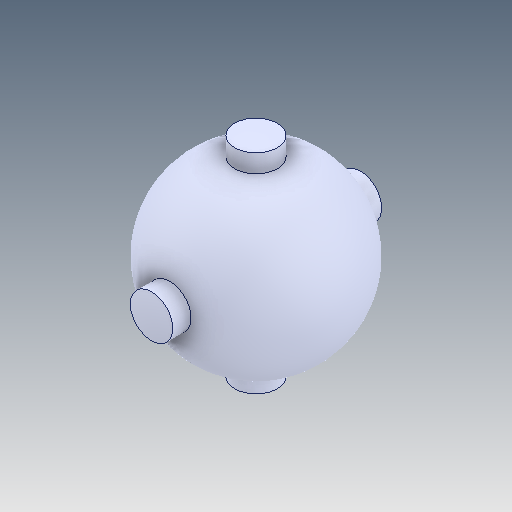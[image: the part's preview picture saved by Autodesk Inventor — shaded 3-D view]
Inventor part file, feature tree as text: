
AUTODESK INVENTOR PART (.ipt)
format: ipt  version: 2020 (Build 240168000, 168)  size: 141,312 bytes
history: mixed  units: in
note: dims shown in document units (in); Inventor stores cm internally (conversion verified against a paired STEP export)
features: revolve x1, imported_body x1
ambient origin geometry x8: Origin, YZ Plane, XZ Plane, XY Plane, X Axis, Y Axis, Z Axis, Center Point
bodies: Solid1 (imported_parasolid)
feature tree (2):
  revolve  "Revolve3"  [1 undecoded]
  imported_body  NMx_Import_Brep_tag  [imported B-rep: ~9 faces, bbox_mm=[2.54, 12.443408, 12.443408]]
note: 1 required parameter value undecoded (feature->parameter linkage not recoverable at this tier; creation-order binding heuristic only, values carry confidence <= 0.55)
